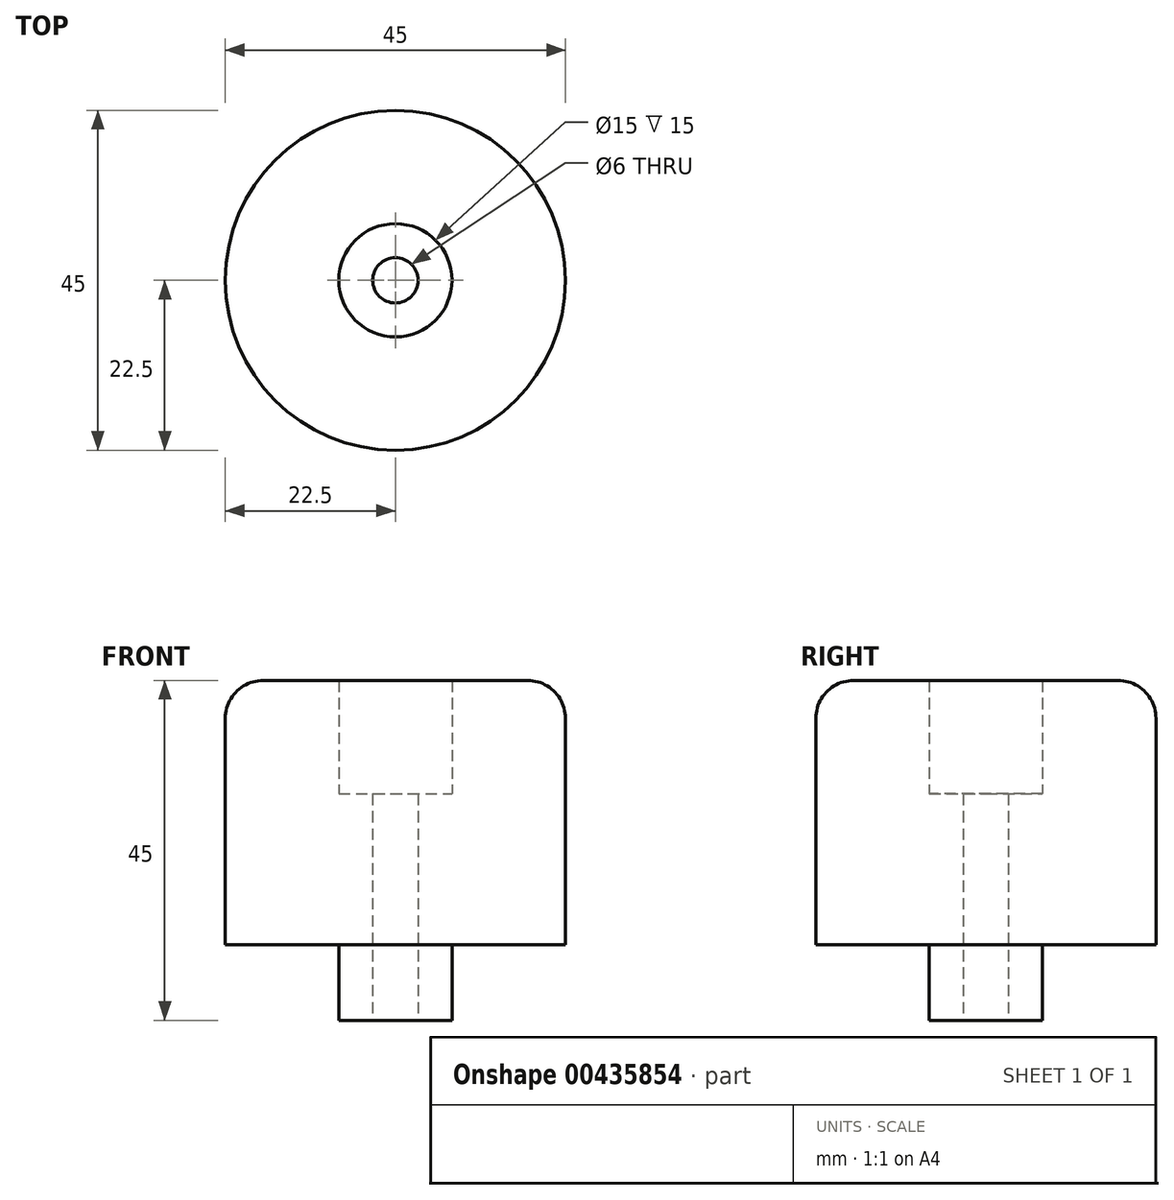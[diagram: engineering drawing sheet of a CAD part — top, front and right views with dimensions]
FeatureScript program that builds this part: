
annotation { "Feature Type Name" : "Feature", "Feature Type Description" : "" }
export const myFeature = defineFeature(function(context is Context, id is Id, definition is map)
    precondition{}
    {
        {
            var Q0;
            Q0=qCreatedBy(makeId("Front.planeOp"),FACE);
            var sketch = newSketch(context, id + "F0", { "sketchPlane" : qUnion([Q0])});
            skLineSegment(sketch, "E0.bottom", {"start": v(0, 0) * mm, "end": v(22.5, 0) * mm});
            skLineSegment(sketch, "E0.top", {"start": v(0, 45) * mm, "end": v(22.5, 45) * mm});
            skLineSegment(sketch, "E0.left", {"start": v(0, 0) * mm, "end": v(0, 45) * mm});
            skLineSegment(sketch, "E0.right", {"start": v(22.5, 0) * mm, "end": v(22.5, 45) * mm});
            skLineSegment(sketch, "E1", {"start": v(0, 10) * mm, "end": v(22.5, 10) * mm});
            skLineSegment(sketch, "E2", {"start": v(0, 30) * mm, "end": v(22.5, 30) * mm});
            skLineSegment(sketch, "E3", {"start": v(3, 45) * mm, "end": v(3, 0) * mm});
            skLineSegment(sketch, "E4", {"start": v(7.5, 45) * mm, "end": v(7.5, 0) * mm});
            skSolve(sketch);
        }
        {
            var Q0;
            {var subQ0=sQuery(id+"F0.wireOp",EDGE,"E0.right");var subQ1=sQuery(id+"F0.wireOp",EDGE,"E0.top");var subQ2=makeQuery(id+"F0.imprint","INTERSECT",VERTEX,{"derivedFrom":[subQ1,subQ0]});Q0=makeQuery(id+"F0.imprint","IMPRINT",FACE,{"disambiguationData":[TD([[makeQuery(id+"F0.imprint","IMPRINT",EDGE,{"disambiguationData":[TD([[subQ2,1.0]])],"derivedFrom":subQ1}),-1.0]])]});}
            var Q1;
            {var subQ0=sQuery(id+"F0.wireOp",EDGE,"E1");var subQ1=sQuery(id+"F0.wireOp",EDGE,"E0.right");var subQ2=makeQuery(id+"F0.imprint","INTERSECT",VERTEX,{"derivedFrom":[subQ1,subQ0]});Q1=makeQuery(id+"F0.imprint","IMPRINT",FACE,{"disambiguationData":[TD([[makeQuery(id+"F0.imprint","IMPRINT",EDGE,{"disambiguationData":[TD([[subQ2,-1.0]])],"derivedFrom":subQ1}),1.0]])]});}
            var Q2;
            {var subQ0=sQuery(id+"F0.wireOp",EDGE,"E3");var subQ1=sQuery(id+"F0.wireOp",EDGE,"E1");var subQ2=makeQuery(id+"F0.imprint","INTERSECT",VERTEX,{"derivedFrom":[subQ1,subQ0]});Q2=makeQuery(id+"F0.imprint","IMPRINT",FACE,{"disambiguationData":[TD([[makeQuery(id+"F0.imprint","IMPRINT",EDGE,{"disambiguationData":[TD([[subQ2,-1.0]])],"derivedFrom":subQ1}),1.0]])]});}
            var Q3;
            {var subQ0=sQuery(id+"F0.wireOp",EDGE,"E3");var subQ1=sQuery(id+"F0.wireOp",EDGE,"E0.bottom");var subQ2=makeQuery(id+"F0.imprint","INTERSECT",VERTEX,{"derivedFrom":[subQ1,subQ0]});Q3=makeQuery(id+"F0.imprint","IMPRINT",FACE,{"disambiguationData":[TD([[makeQuery(id+"F0.imprint","IMPRINT",EDGE,{"disambiguationData":[TD([[subQ2,-1.0]])],"derivedFrom":subQ1}),1.0]])]});}
            var Q4;
            Q4=sQuery(id+"F0.wireOp",EDGE,"E0.left");
            revolve(context, id + "F1", {"entities" : qUnion([Q0, Q1, Q2, Q3]), "axis" : qUnion([Q4]), "revolveType" : RevolveType.FULL});
        }
        {
            var Q0;
            Q0=makeQuery(id+"F1.opRevolve","SWEPT_EDGE",EDGE,{"disambiguationData":[OSD([sQuery(id+"F0.wireOp",EDGE,"E0.top"),sQuery(id+"F0.wireOp",EDGE,"E0.right")])]});
            fillet(context, id + "F2", {"entities" : qUnion([Q0]), "radius" : 5 * mm, "tangentPropagation" : true, "allowEdgeOverflow" : false});
        }
    });
